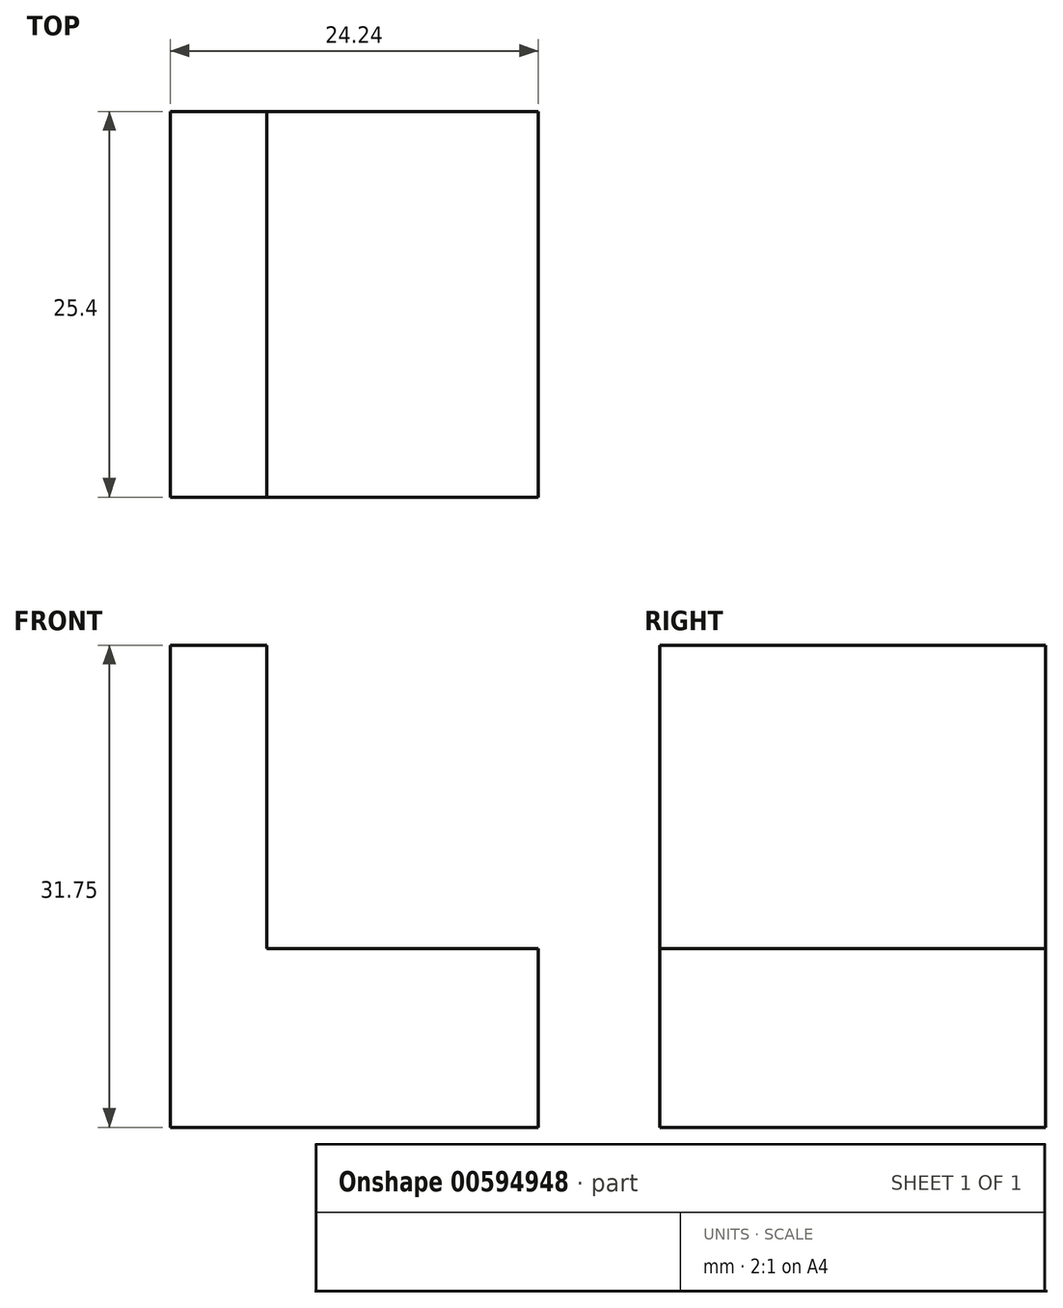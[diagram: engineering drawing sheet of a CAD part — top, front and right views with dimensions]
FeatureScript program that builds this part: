
annotation { "Feature Type Name" : "Feature", "Feature Type Description" : "" }
export const myFeature = defineFeature(function(context is Context, id is Id, definition is map)
    precondition{}
    {
        {
            var Q0;
            Q0=qCreatedBy(makeId("Front.planeOp"),FACE);
            var sketch = newSketch(context, id + "F0", { "sketchPlane" : qUnion([Q0])});
            skLineSegment(sketch, "E0", {"start": v(0, 0) * mm, "end": v(0, 31.75) * mm});
            skLineSegment(sketch, "E1", {"start": v(0, 31.75) * mm, "end": v(6.35, 31.75) * mm});
            skLineSegment(sketch, "E2", {"start": v(6.35, 31.75) * mm, "end": v(6.35, 11.78) * mm});
            skLineSegment(sketch, "E3", {"start": v(6.35, 11.78) * mm, "end": v(24.24, 11.78) * mm});
            skLineSegment(sketch, "E4", {"start": v(24.24, 11.78) * mm, "end": v(24.24, 0) * mm});
            skLineSegment(sketch, "E5", {"start": v(24.24, 0) * mm, "end": v(0, 0) * mm});
            skSolve(sketch);
        }
        {
            var Q0;
            Q0 = qSketchRegion(id + "F0", true);
            extrude(context, id + "F1", {"entities" : qUnion([Q0]), "depth" : 25.4 * mm, "offsetDistance" : 25.4 * mm});
        }
    });
